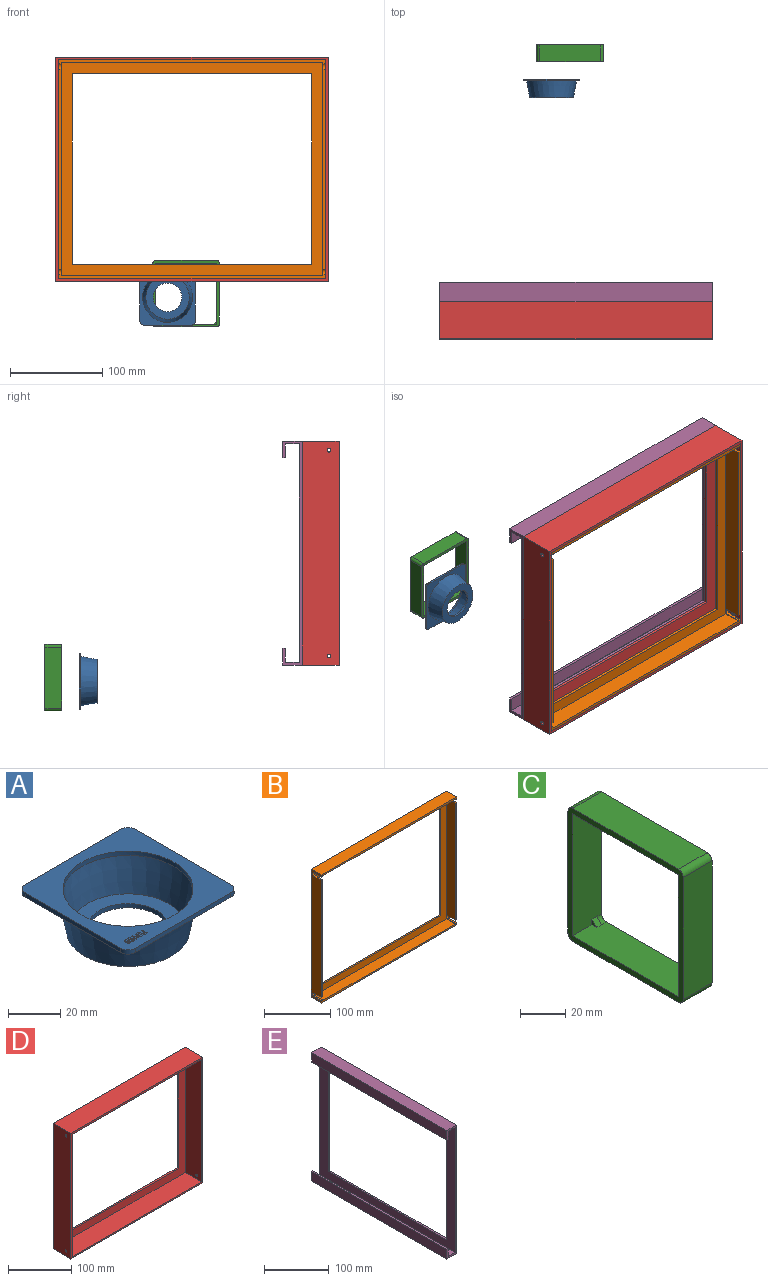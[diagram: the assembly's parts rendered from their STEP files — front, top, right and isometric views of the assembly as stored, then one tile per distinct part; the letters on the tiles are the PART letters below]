
ASSEMBLY  parts=5 mates=4
PART A: 101 faces, bbox 60x60x20 mm
  f0: plane 60x60mm, normal (0,0,1), area 1612.5mm2, adj f1,f2,f3,f4,f5,f7,f8,f9
  f1: plane 52x2mm, normal (1,0,0), area 104mm2, adj f0,f6,f7,f10
  f2: plane 52x2mm, normal (0,1,0), area 104mm2, adj f0,f6,f7,f8
  f3: plane 52x2mm, normal (-1,0,0), area 104mm2, adj f0,f6,f8,f9
  f4: plane 52x2mm, normal (0,-1,0), area 104mm2, adj f0,f6,f9,f10
  f5: cylinder r=25mm len=50mm, axis (0,0,-1), area 314.2mm2, adj f0,f14
  f6: plane 60x60mm, normal (0,0,-1), area 1288.6mm2, adj f1,f2,f3,f4,f7,f8,f9,f10
  f7: cylinder r=4mm len=4mm, axis (0,0,1), area 12.6mm2, adj f0,f1,f2,f6
  f8: cylinder r=4mm len=4mm, axis (0,0,-1), area 12.6mm2, adj f0,f2,f3,f6
  f9: cylinder r=4mm len=4mm, axis (0,0,1), area 12.6mm2, adj f0,f3,f4,f6
  f10: cylinder r=4mm len=4mm, axis (0,0,-1), area 12.6mm2, adj f0,f1,f4,f6
  f11: cylinder r=15.5mm len=31mm, axis (0,0,-1), area 194.8mm2, adj f12,f15
  f12: plane 47.23x47.23mm, normal (0,0,-1), area 996.8mm2, adj f11,f13
  f13: cone r=23.61mm half-angle=10.8deg, axis (0,0,1), area 2908.4mm2, adj f6,f12
  f14: cone r=21.96mm half-angle=10.8deg, axis (0,0,1), area 2396.1mm2, adj f5,f15
  f15: plane 43.92x43.92mm, normal (0,0,1), area 760mm2, adj f11,f14
  f16: extruded ~0.65x0.21mm, area 0.1mm2, adj f0,f17,f34,f35
  f17: extruded ~0.41x0.1mm, area 0mm2, adj f0,f16,f18,f35
  f18: plane 0.79x0.1mm, normal (-1,0.08,0), area 0.1mm2, adj f0,f17,f19,f35
  f19: plane 1.05x0.1mm, normal (0,1,0), area 0.1mm2, adj f0,f18,f20,f35
  f20: plane 0.27x0.1mm, normal (-1,0,0), area 0mm2, adj f0,f19,f21,f35
  f21: plane 1.3x0.1mm, normal (0,-1,0), area 0.1mm2, adj f0,f20,f22,f35
  f22: plane 1.23x0.1mm, normal (1,-0.08,0), area 0.1mm2, adj f0,f21,f23,f35
  f23: plane 0.15x0.1mm, normal (0.54,0.84,0), area 0mm2, adj f0,f22,f24,f35
  f24: extruded ~0.46x0.1mm, area 0mm2, adj f0,f23,f25,f35
  f25: extruded ~0.67x0.55mm, area 0.1mm2, adj f0,f24,f26,f35
  f26: extruded ~0.43x0.17mm, area 0mm2, adj f0,f25,f27,f35
  f27: extruded ~0.49x0.15mm, area 0.1mm2, adj f0,f26,f28,f35
  f28: extruded ~0.37x0.1mm, area 0mm2, adj f0,f27,f29,f35
  f29: extruded ~0.31x0.13mm, area 0mm2, adj f0,f28,f30,f35
  f30: plane 0.29x0.1mm, normal (1,0,0), area 0mm2, adj f0,f29,f31,f35
  f31: extruded ~0.68x0.14mm, area 0.1mm2, adj f0,f30,f32,f35
  f32: extruded ~0.71x0.23mm, area 0.1mm2, adj f0,f31,f33,f35
  f33: extruded ~0.64x0.26mm, area 0.1mm2, adj f0,f32,f34,f35
  f34: extruded ~0.56x0.24mm, area 0.1mm2, adj f0,f16,f33,f35
  f35: plane 2.65x1.65mm, normal (0,0,1), area 1.6mm2, adj f16,f17,f18,f19,f20,f21,f22,f23
  f36: plane 2.32x0.89mm, normal (0.93,0.36,0), area 0.2mm2, adj f0,f37,f53,f54
  f37: plane 0.25x0.1mm, normal (0,1,0), area 0mm2, adj f0,f36,f38,f54
  f38: plane 2.32x0.9mm, normal (-0.93,0.36,0), area 0.2mm2, adj f0,f37,f39,f54
  f39: plane 0.1x0.01mm, normal (0,1,0), area 0mm2, adj f0,f38,f40,f54
  f40: extruded ~0.63x0.1mm, area 0.1mm2, adj f0,f39,f41,f54
  f41: plane 1.69x0.1mm, normal (1,0,0), area 0.2mm2, adj f0,f40,f42,f54
  f42: plane 0.3x0.1mm, normal (0,1,0), area 0mm2, adj f0,f41,f43,f54
  f43: plane 2.62x0.1mm, normal (-1,0,0), area 0.3mm2, adj f0,f42,f44,f54
  f44: plane 0.46x0.1mm, normal (0,-1,0), area 0mm2, adj f0,f43,f45,f54
  f45: plane 2.16x0.84mm, normal (0.93,-0.36,0), area 0.2mm2, adj f0,f44,f46,f54
  f46: plane 0.1x0.01mm, normal (0,-1,0), area 0mm2, adj f0,f45,f47,f54
  f47: plane 2.16x0.83mm, normal (-0.93,-0.36,0), area 0.2mm2, adj f0,f46,f48,f54
  f48: plane 0.46x0.1mm, normal (0,-1,0), area 0mm2, adj f0,f47,f49,f54
  f49: plane 2.62x0.1mm, normal (1,0,0), area 0.3mm2, adj f0,f48,f50,f54
  f50: plane 0.28x0.1mm, normal (0,1,0), area 0mm2, adj f0,f49,f51,f54
  f51: plane 1.67x0.1mm, normal (-1,0,0), area 0.2mm2, adj f0,f50,f52,f54
  f52: extruded ~0.66x0.1mm, area 0.1mm2, adj f0,f51,f53,f54
  f53: plane 0.1x0.01mm, normal (0,1,0), area 0mm2, adj f0,f36,f52,f54
  f54: plane 2.62x2.59mm, normal (0,0,1), area 2.9mm2, adj f36,f37,f38,f39,f40,f41,f42,f43
  f55: plane 2.32x0.89mm, normal (0.93,0.36,0), area 0.2mm2, adj f0,f56,f72,f73
  f56: plane 0.25x0.1mm, normal (0,1,0), area 0mm2, adj f0,f55,f57,f73
  f57: plane 2.32x0.9mm, normal (-0.93,0.36,0), area 0.2mm2, adj f0,f56,f58,f73
  f58: plane 0.1x0.01mm, normal (0,1,0), area 0mm2, adj f0,f57,f59,f73
  f59: extruded ~0.63x0.1mm, area 0.1mm2, adj f0,f58,f60,f73
  f60: plane 1.69x0.1mm, normal (1,0,0), area 0.2mm2, adj f0,f59,f61,f73
  f61: plane 0.3x0.1mm, normal (0,1,0), area 0mm2, adj f0,f60,f62,f73
  f62: plane 2.62x0.1mm, normal (-1,0,0), area 0.3mm2, adj f0,f61,f63,f73
  f63: plane 0.46x0.1mm, normal (0,-1,0), area 0mm2, adj f0,f62,f64,f73
  f64: plane 2.16x0.84mm, normal (0.93,-0.36,0), area 0.2mm2, adj f0,f63,f65,f73
  f65: plane 0.1x0.01mm, normal (0,-1,0), area 0mm2, adj f0,f64,f66,f73
  f66: plane 2.16x0.83mm, normal (-0.93,-0.36,0), area 0.2mm2, adj f0,f65,f67,f73
  f67: plane 0.46x0.1mm, normal (0,-1,0), area 0mm2, adj f0,f66,f68,f73
  f68: plane 2.62x0.1mm, normal (1,0,0), area 0.3mm2, adj f0,f67,f69,f73
  f69: plane 0.28x0.1mm, normal (0,1,0), area 0mm2, adj f0,f68,f70,f73
  f70: plane 1.67x0.1mm, normal (-1,0,0), area 0.2mm2, adj f0,f69,f71,f73
  f71: extruded ~0.66x0.1mm, area 0.1mm2, adj f0,f70,f72,f73
  f72: plane 0.1x0.01mm, normal (0,1,0), area 0mm2, adj f0,f55,f71,f73
  f73: plane 2.62x2.59mm, normal (0,0,1), area 2.9mm2, adj f55,f56,f57,f58,f59,f60,f61,f62
  f74: extruded ~0.39x0.16mm, area 0mm2, adj f75,f98,f99,f100
  f75: extruded ~0.3x0.1mm, area 0mm2, adj f74,f76,f99,f100
  f76: extruded ~0.25x0.2mm, area 0mm2, adj f75,f77,f99,f100
  f77: extruded ~0.34x0.1mm, area 0mm2, adj f76,f78,f99,f100
  f78: extruded ~0.24x0.1mm, area 0mm2, adj f77,f79,f99,f100
  f79: extruded ~0.21x0.18mm, area 0mm2, adj f78,f80,f99,f100
  f80: extruded ~0.3x0.1mm, area 0mm2, adj f79,f81,f99,f100
  f81: extruded ~0.39x0.15mm, area 0mm2, adj f80,f82,f99,f100
  f82: extruded ~0.41x0.13mm, area 0mm2, adj f81,f98,f99,f100
  f83: extruded ~1.15x0.3mm, area 0.1mm2, adj f0,f84,f97,f99
  f84: extruded ~0.85x0.24mm, area 0.1mm2, adj f0,f83,f85,f99
  f85: extruded ~0.64x0.31mm, area 0.1mm2, adj f0,f84,f86,f99
  f86: extruded ~0.6x0.23mm, area 0.1mm2, adj f0,f85,f87,f99
  f87: extruded ~0.64x0.22mm, area 0.1mm2, adj f0,f86,f88,f99
  f88: extruded ~0.58x0.2mm, area 0.1mm2, adj f0,f87,f89,f99
  f89: extruded ~0.56x0.21mm, area 0.1mm2, adj f0,f88,f90,f99
  f90: extruded ~0.62x0.31mm, area 0.1mm2, adj f0,f89,f91,f99
  f91: plane 0.1x0.02mm, normal (0,-1,0), area 0mm2, adj f0,f90,f92,f99
  f92: extruded ~0.83x0.24mm, area 0.1mm2, adj f0,f91,f93,f99
  f93: extruded ~0.64x0.26mm, area 0.1mm2, adj f0,f92,f94,f99
  f94: extruded ~0.32x0.1mm, area 0mm2, adj f0,f93,f95,f99
  f95: plane 0.26x0.1mm, normal (-1,0,0), area 0mm2, adj f0,f94,f96,f99
  f96: extruded ~0.32x0.1mm, area 0mm2, adj f0,f95,f97,f99
  f97: extruded ~0.89x0.38mm, area 0.1mm2, adj f0,f83,f96,f99
  f98: extruded ~0.46x0.14mm, area 0mm2, adj f74,f82,f99,f100
  f99: plane 2.69x1.71mm, normal (0,0,1), area 1.8mm2, adj f74,f75,f76,f77,f78,f79,f80,f81
  f100: plane 1.18x1.11mm, normal (0,0,1), area 1.1mm2, adj f74,f75,f76,f77,f78,f79,f80,f81
PART B: 126 faces, bbox 289.3x22x236.8 mm
  f0: plane 289.28x4mm, normal (0,-1,0), area 873.8mm2, adj f3,f4,f13,f30,f41,f44,f69,f109
  f1: plane 216.71x3mm, normal (0,-1,0), area 650.1mm2, adj f3,f5,f90,f107
  f2: plane 216.71x3mm, normal (0,-1,0), area 650.1mm2, adj f4,f22,f50,f87
  f3: plane 236.78x22mm, normal (1,0,0), area 4975mm2, adj f0,f1,f39,f40,f41,f42,f88,f89
  f4: plane 236.78x22mm, normal (-1,0,0), area 4975mm2, adj f0,f2,f39,f40,f41,f42,f50,f51
  f5: plane 230.78x19mm, normal (-1,0,0), area 4134.3mm2, adj f1,f43,f44,f45,f88,f89,f90,f107
  f6: plane 2x1mm, normal (-1,0,0), area 1mm2, adj f44,f111,f112
  f7: plane 2x1mm, normal (-1,0,0), area 1mm2, adj f44,f113,f114
  f8: plane 2x1mm, normal (-1,0,0), area 1mm2, adj f44,f115,f116
  f9: plane 2x1mm, normal (-1,0,0), area 1mm2, adj f44,f117,f118
  f10: plane 2x1mm, normal (-1,0,0), area 1mm2, adj f44,f119,f120
  f11: plane 2x1mm, normal (-1,0,0), area 1mm2, adj f44,f121,f122
  f12: plane 2x1mm, normal (-1,0,0), area 1mm2, adj f44,f123,f124
  f13: plane 1.65x1mm, normal (-1,0,0), area 1.2mm2, adj f0,f44,f109,f125
  f14: plane 1.65x1mm, normal (-1,0,0), area 1.2mm2, adj f39,f43,f91,f92
  f15: plane 2x1mm, normal (-1,0,0), area 1mm2, adj f43,f93,f94
  f16: plane 2x1mm, normal (-1,0,0), area 1mm2, adj f43,f95,f96
  f17: plane 2x1mm, normal (-1,0,0), area 1mm2, adj f43,f97,f98
  f18: plane 2x1mm, normal (-1,0,0), area 1mm2, adj f43,f99,f100
  f19: plane 2x1mm, normal (-1,0,0), area 1mm2, adj f43,f101,f102
  f20: plane 2x1mm, normal (-1,0,0), area 1mm2, adj f43,f103,f104
  f21: plane 2x1mm, normal (-1,0,0), area 1mm2, adj f43,f105,f106
  f22: plane 230.78x19mm, normal (1,0,0), area 4134.3mm2, adj f2,f43,f44,f45,f50,f51,f68,f85
  f23: plane 2x1mm, normal (1,0,0), area 1mm2, adj f44,f83,f84
  f24: plane 2x1mm, normal (1,0,0), area 1mm2, adj f44,f81,f82
  f25: plane 2x1mm, normal (1,0,0), area 1mm2, adj f44,f79,f80
  f26: plane 2x1mm, normal (1,0,0), area 1mm2, adj f44,f77,f78
  f27: plane 2x1mm, normal (1,0,0), area 1mm2, adj f44,f75,f76
  f28: plane 2x1mm, normal (1,0,0), area 1mm2, adj f44,f73,f74
  f29: plane 2x1mm, normal (1,0,0), area 1mm2, adj f44,f71,f72
  f30: plane 1.65x1mm, normal (1,0,0), area 1.2mm2, adj f0,f44,f69,f70
  f31: plane 1.65x1mm, normal (1,0,0), area 1.2mm2, adj f39,f43,f66,f67
  f32: plane 2x1mm, normal (1,0,0), area 1mm2, adj f43,f64,f65
  f33: plane 2x1mm, normal (1,0,0), area 1mm2, adj f43,f62,f63
  f34: plane 2x1mm, normal (1,0,0), area 1mm2, adj f43,f60,f61
  f35: plane 2x1mm, normal (1,0,0), area 1mm2, adj f43,f58,f59
  f36: plane 2x1mm, normal (1,0,0), area 1mm2, adj f43,f56,f57
  f37: plane 2x1mm, normal (1,0,0), area 1mm2, adj f43,f54,f55
  f38: plane 2x1mm, normal (1,0,0), area 1mm2, adj f43,f52,f53
  f39: plane 289.28x4mm, normal (0,-1,0), area 873.8mm2, adj f3,f4,f14,f31,f40,f43,f67,f91
  f40: plane 289.28x22mm, normal (0,0,1), area 6364.1mm2, adj f3,f4,f39,f42
  f41: plane 289.28x22mm, normal (0,0,-1), area 6364.1mm2, adj f0,f3,f4,f42
  f42: plane 289.28x236.78mm, normal (0,1,0), area 14881.6mm2, adj f3,f4,f40,f41,f46,f47,f48,f49
  f43: plane 283.28x19mm, normal (0,0,-1), area 5382.2mm2, adj f5,f14,f15,f16,f17,f18,f19,f20
  f44: plane 283.28x19mm, normal (0,0,1), area 5382.2mm2, adj f0,f5,f6,f7,f8,f9,f10,f11
  f45: plane 283.28x230.78mm, normal (0,-1,0), area 11761.3mm2, adj f5,f22,f43,f44,f46,f47,f48,f49
  f46: plane 206.78x3mm, normal (-1,0,0), area 620.3mm2, adj f42,f45,f47,f49
  f47: plane 259.28x3mm, normal (0,0,-1), area 777.8mm2, adj f42,f45,f46,f48
  f48: plane 206.78x3mm, normal (1,0,0), area 620.3mm2, adj f42,f45,f47,f49
  f49: plane 259.28x3mm, normal (0,0,1), area 777.8mm2, adj f42,f45,f46,f48
  f50: plane 16.65x3mm, normal (0,0,1), area 50mm2, adj f2,f4,f22,f51
  f51: cylinder r=3.3mm len=6.04mm, axis (-1,0,0), area 22.9mm2, adj f4,f22,f50,f68
  f52: plane 3x1mm, normal (0,0.71,-0.71), area 4.2mm2, adj f4,f38,f53,f68
  f53: plane 3x1mm, normal (0,-0.71,-0.71), area 4.2mm2, adj f4,f38,f52,f54
  f54: plane 3x1mm, normal (0,0.71,-0.71), area 4.2mm2, adj f4,f37,f53,f55
  f55: plane 3x1mm, normal (0,-0.71,-0.71), area 4.2mm2, adj f4,f37,f54,f56
  f56: plane 3x1mm, normal (0,0.71,-0.71), area 4.2mm2, adj f4,f36,f55,f57
  f57: plane 3x1mm, normal (0,-0.71,-0.71), area 4.2mm2, adj f4,f36,f56,f58
  f58: plane 3x1mm, normal (0,0.71,-0.71), area 4.2mm2, adj f4,f35,f57,f59
  f59: plane 3x1mm, normal (0,-0.71,-0.71), area 4.2mm2, adj f4,f35,f58,f60
  f60: plane 3x1mm, normal (0,0.71,-0.71), area 4.2mm2, adj f4,f34,f59,f61
  f61: plane 3x1mm, normal (0,-0.71,-0.71), area 4.2mm2, adj f4,f34,f60,f62
  f62: plane 3x1mm, normal (0,0.71,-0.71), area 4.2mm2, adj f4,f33,f61,f63
  f63: plane 3x1mm, normal (0,-0.71,-0.71), area 4.2mm2, adj f4,f33,f62,f64
  f64: plane 3x1mm, normal (0,0.71,-0.71), area 4.2mm2, adj f4,f32,f63,f65
  f65: plane 3x1mm, normal (0,-0.71,-0.71), area 4.2mm2, adj f4,f32,f64,f66
  f66: plane 3x1mm, normal (0,0.71,-0.71), area 4.2mm2, adj f4,f31,f65,f67
  f67: plane 3x0.65mm, normal (0,0,-1), area 2mm2, adj f4,f31,f39,f66
  f68: plane 3x1mm, normal (0,-0.71,-0.71), area 4.2mm2, adj f4,f22,f51,f52
  f69: plane 3x0.65mm, normal (0,0,1), area 2mm2, adj f0,f4,f30,f70
  f70: plane 3x1mm, normal (0,0.71,0.71), area 4.2mm2, adj f4,f30,f69,f71
  f71: plane 3x1mm, normal (0,-0.71,0.71), area 4.2mm2, adj f4,f29,f70,f72
  f72: plane 3x1mm, normal (0,0.71,0.71), area 4.2mm2, adj f4,f29,f71,f73
  f73: plane 3x1mm, normal (0,-0.71,0.71), area 4.2mm2, adj f4,f28,f72,f74
  f74: plane 3x1mm, normal (0,0.71,0.71), area 4.2mm2, adj f4,f28,f73,f75
  f75: plane 3x1mm, normal (0,-0.71,0.71), area 4.2mm2, adj f4,f27,f74,f76
  f76: plane 3x1mm, normal (0,0.71,0.71), area 4.2mm2, adj f4,f27,f75,f77
  f77: plane 3x1mm, normal (0,-0.71,0.71), area 4.2mm2, adj f4,f26,f76,f78
  f78: plane 3x1mm, normal (0,0.71,0.71), area 4.2mm2, adj f4,f26,f77,f79
  f79: plane 3x1mm, normal (0,-0.71,0.71), area 4.2mm2, adj f4,f25,f78,f80
  f80: plane 3x1mm, normal (0,0.71,0.71), area 4.2mm2, adj f4,f25,f79,f81
  f81: plane 3x1mm, normal (0,-0.71,0.71), area 4.2mm2, adj f4,f24,f80,f82
  f82: plane 3x1mm, normal (0,0.71,0.71), area 4.2mm2, adj f4,f24,f81,f83
  f83: plane 3x1mm, normal (0,-0.71,0.71), area 4.2mm2, adj f4,f23,f82,f84
  f84: plane 3x1mm, normal (0,0.71,0.71), area 4.2mm2, adj f4,f23,f83,f85
  f85: plane 3x1mm, normal (0,-0.71,0.71), area 4.2mm2, adj f4,f22,f84,f86
  f86: cylinder r=3.3mm len=6.04mm, axis (-1,0,0), area 22.9mm2, adj f4,f22,f85,f87
  f87: plane 16.65x3mm, normal (0,0,-1), area 50mm2, adj f2,f4,f22,f86
  f88: plane 3x1mm, normal (0,-0.71,-0.71), area 4.2mm2, adj f3,f5,f89,f106
  f89: cylinder r=3.3mm len=6.04mm, axis (-1,0,0), area 22.9mm2, adj f3,f5,f88,f90
  f90: plane 16.65x3mm, normal (0,0,1), area 50mm2, adj f1,f3,f5,f89
  f91: plane 3x0.65mm, normal (0,0,-1), area 2mm2, adj f3,f14,f39,f92
  f92: plane 3x1mm, normal (0,0.71,-0.71), area 4.2mm2, adj f3,f14,f91,f93
  f93: plane 3x1mm, normal (0,-0.71,-0.71), area 4.2mm2, adj f3,f15,f92,f94
  f94: plane 3x1mm, normal (0,0.71,-0.71), area 4.2mm2, adj f3,f15,f93,f95
  f95: plane 3x1mm, normal (0,-0.71,-0.71), area 4.2mm2, adj f3,f16,f94,f96
  f96: plane 3x1mm, normal (0,0.71,-0.71), area 4.2mm2, adj f3,f16,f95,f97
  f97: plane 3x1mm, normal (0,-0.71,-0.71), area 4.2mm2, adj f3,f17,f96,f98
  f98: plane 3x1mm, normal (0,0.71,-0.71), area 4.2mm2, adj f3,f17,f97,f99
  f99: plane 3x1mm, normal (0,-0.71,-0.71), area 4.2mm2, adj f3,f18,f98,f100
  f100: plane 3x1mm, normal (0,0.71,-0.71), area 4.2mm2, adj f3,f18,f99,f101
  f101: plane 3x1mm, normal (0,-0.71,-0.71), area 4.2mm2, adj f3,f19,f100,f102
  f102: plane 3x1mm, normal (0,0.71,-0.71), area 4.2mm2, adj f3,f19,f101,f103
  f103: plane 3x1mm, normal (0,-0.71,-0.71), area 4.2mm2, adj f3,f20,f102,f104
  f104: plane 3x1mm, normal (0,0.71,-0.71), area 4.2mm2, adj f3,f20,f103,f105
  f105: plane 3x1mm, normal (0,-0.71,-0.71), area 4.2mm2, adj f3,f21,f104,f106
  f106: plane 3x1mm, normal (0,0.71,-0.71), area 4.2mm2, adj f3,f21,f88,f105
  f107: plane 16.65x3mm, normal (0,0,-1), area 50mm2, adj f1,f3,f5,f108
  f108: cylinder r=3.3mm len=6.04mm, axis (-1,0,0), area 22.9mm2, adj f3,f5,f107,f110
  f109: plane 3x0.65mm, normal (0,0,1), area 2mm2, adj f0,f3,f13,f125
  f110: plane 3x1mm, normal (0,-0.71,0.71), area 4.2mm2, adj f3,f5,f108,f111
  f111: plane 3x1mm, normal (0,0.71,0.71), area 4.2mm2, adj f3,f6,f110,f112
  f112: plane 3x1mm, normal (0,-0.71,0.71), area 4.2mm2, adj f3,f6,f111,f113
  f113: plane 3x1mm, normal (0,0.71,0.71), area 4.2mm2, adj f3,f7,f112,f114
  f114: plane 3x1mm, normal (0,-0.71,0.71), area 4.2mm2, adj f3,f7,f113,f115
  f115: plane 3x1mm, normal (0,0.71,0.71), area 4.2mm2, adj f3,f8,f114,f116
  f116: plane 3x1mm, normal (0,-0.71,0.71), area 4.2mm2, adj f3,f8,f115,f117
  f117: plane 3x1mm, normal (0,0.71,0.71), area 4.2mm2, adj f3,f9,f116,f118
  f118: plane 3x1mm, normal (0,-0.71,0.71), area 4.2mm2, adj f3,f9,f117,f119
  f119: plane 3x1mm, normal (0,0.71,0.71), area 4.2mm2, adj f3,f10,f118,f120
  f120: plane 3x1mm, normal (0,-0.71,0.71), area 4.2mm2, adj f3,f10,f119,f121
  f121: plane 3x1mm, normal (0,0.71,0.71), area 4.2mm2, adj f3,f11,f120,f122
  f122: plane 3x1mm, normal (0,-0.71,0.71), area 4.2mm2, adj f3,f11,f121,f123
  f123: plane 3x1mm, normal (0,0.71,0.71), area 4.2mm2, adj f3,f12,f122,f124
  f124: plane 3x1mm, normal (0,-0.71,0.71), area 4.2mm2, adj f3,f12,f123,f125
  f125: plane 3x1mm, normal (0,0.71,0.71), area 4.2mm2, adj f3,f13,f109,f124
PART C: 30 faces, bbox 18x72x72 mm
  f0: plane 3x3mm, normal (-1,0,0), area 4.5mm2, adj f12,f15,f29
  f1: plane 3x3mm, normal (-1,0,0), area 4.5mm2, adj f12,f13,f28
  f2: plane 3x3mm, normal (-1,0,0), area 4.5mm2, adj f13,f14,f27
  f3: plane 3x3mm, normal (1,0,0), area 2.6mm2, adj f19,f26
  f4: plane 3x3mm, normal (1,0,0), area 2.6mm2, adj f20,f27
  f5: plane 3x3mm, normal (1,0,0), area 2.6mm2, adj f21,f28
  f6: plane 66x18mm, normal (0,1,0), area 1188mm2, adj f10,f11,f22,f25
  f7: plane 66x18mm, normal (0,0,1), area 1188mm2, adj f10,f11,f22,f23
  f8: plane 66x18mm, normal (0,-1,0), area 1188mm2, adj f10,f11,f23,f24
  f9: plane 66x18mm, normal (0,0,-1), area 1188mm2, adj f10,f11,f24,f25
  f10: plane 72x72mm, normal (1,0,0), area 828mm2, adj f6,f7,f8,f9,f12,f13,f14,f15
  f11: plane 72x72mm, normal (-1,0,0), area 820.3mm2, adj f6,f7,f8,f9,f12,f13,f14,f15
  f12: plane 66x18mm, normal (0,-1,0), area 1152mm2, adj f0,f1,f10,f11,f13,f15,f18,f21
  f13: plane 66x18mm, normal (0,0,1), area 1152mm2, adj f1,f2,f10,f11,f12,f14,f20,f21
  f14: plane 66x18mm, normal (0,1,0), area 1152mm2, adj f2,f10,f11,f13,f15,f16,f19,f20
  f15: plane 66x18mm, normal (0,0,-1), area 1152mm2, adj f0,f10,f11,f12,f14,f16,f18,f19
  f16: plane 3x3mm, normal (-1,0,0), area 4.5mm2, adj f14,f15,f26
  f17: plane 3x3mm, normal (1,0,0), area 2.6mm2, adj f18,f29
  f18: cylinder r=3mm len=3mm, axis (-1,0,0), area 14.1mm2, adj f10,f12,f15,f17
  f19: cylinder r=3mm len=3mm, axis (-1,0,0), area 14.1mm2, adj f3,f10,f14,f15
  f20: cylinder r=3mm len=3mm, axis (-1,0,0), area 14.1mm2, adj f4,f10,f13,f14
  f21: cylinder r=3mm len=3mm, axis (-1,0,0), area 14.1mm2, adj f5,f10,f12,f13
  f22: cylinder r=3mm len=18mm, axis (1,0,0), area 84.8mm2, adj f6,f7,f10,f11
  f23: cylinder r=3mm len=18mm, axis (-1,0,0), area 84.8mm2, adj f7,f8,f10,f11
  f24: cylinder r=3mm len=18mm, axis (1,0,0), area 84.8mm2, adj f8,f9,f10,f11
  f25: cylinder r=3mm len=18mm, axis (-1,0,0), area 84.8mm2, adj f6,f9,f10,f11
  f26: plane 3x3mm, normal (0,0.71,-0.71), area 12.7mm2, adj f3,f14,f15,f16
  f27: plane 3x3mm, normal (0,0.71,0.71), area 12.7mm2, adj f2,f4,f13,f14
  f28: plane 3x3mm, normal (0,-0.71,0.71), area 12.7mm2, adj f1,f5,f12,f13
  f29: plane 3x3mm, normal (0,-0.71,-0.71), area 12.7mm2, adj f0,f12,f15,f17
PART D: 19 faces, bbox 295.3x40x242.8 mm
  f0: plane 295.28x242.78mm, normal (0,-1,0), area 3192.3mm2, adj f1,f2,f3,f4,f6,f7,f8,f9
  f1: plane 242.78x40mm, normal (1,0,0), area 9686mm2, adj f0,f2,f4,f5,f17,f18
  f2: plane 295.28x40mm, normal (0,0,1), area 11811mm2, adj f0,f1,f3,f5
  f3: plane 242.78x40mm, normal (-1,0,0), area 9686mm2, adj f0,f2,f4,f5,f15,f16
  f4: plane 295.28x40mm, normal (0,0,-1), area 11811mm2, adj f0,f1,f3,f5
  f5: plane 295.28x242.78mm, normal (0,1,0), area 18073.9mm2, adj f1,f2,f3,f4,f11,f12,f13,f14
  f6: plane 236.78x37mm, normal (-1,0,0), area 8735.7mm2, adj f0,f7,f9,f10,f17,f18
  f7: plane 289.28x37mm, normal (0,0,-1), area 10703.2mm2, adj f0,f6,f8,f10
  f8: plane 236.78x37mm, normal (1,0,0), area 8735.7mm2, adj f0,f7,f9,f10,f15,f16
  f9: plane 289.28x37mm, normal (0,0,1), area 10703.2mm2, adj f0,f6,f8,f10
  f10: plane 289.28x236.78mm, normal (0,-1,0), area 14881.6mm2, adj f6,f7,f8,f9,f11,f12,f13,f14
  f11: plane 206.78x3mm, normal (-1,0,0), area 620.3mm2, adj f5,f10,f12,f14
  f12: plane 259.28x3mm, normal (0,0,-1), area 777.8mm2, adj f5,f10,f11,f13
  f13: plane 206.78x3mm, normal (1,0,0), area 620.3mm2, adj f5,f10,f12,f14
  f14: plane 259.28x3mm, normal (0,0,1), area 777.8mm2, adj f5,f10,f11,f13
  f15: cylinder r=2mm len=4mm, axis (-1,0,0), area 37.7mm2, adj f3,f8
  f16: cylinder r=2mm len=4mm, axis (-1,0,0), area 37.7mm2, adj f3,f8
  f17: cylinder r=2mm len=4mm, axis (-1,0,0), area 37.7mm2, adj f1,f6
  f18: cylinder r=2mm len=4mm, axis (-1,0,0), area 37.7mm2, adj f1,f6
PART E: 18 faces, bbox 21.1x295.3x242.8 mm
  f0: plane 295.28x242.78mm, normal (1,0,0), area 18073.9mm2, adj f1,f11,f12,f13,f14,f15,f16,f17
  f1: plane 295.28x21.1mm, normal (0,0,1), area 6230.3mm2, adj f0,f2,f12,f13
  f2: plane 295.28x18mm, normal (-1,0,0), area 5314.9mm2, adj f1,f3,f12,f13
  f3: plane 295.28x3mm, normal (0,0,-1), area 885.8mm2, adj f2,f4,f12,f13
  f4: plane 295.28x15mm, normal (1,0,0), area 4429.1mm2, adj f3,f5,f12,f13
  f5: plane 295.28x15.1mm, normal (0,0,-1), area 4458.7mm2, adj f4,f6,f12,f13
  f6: plane 295.28x236.78mm, normal (-1,0,0), area 16302.3mm2, adj f5,f7,f12,f13,f14,f15,f16,f17
  f7: plane 295.28x15.1mm, normal (0,0,1), area 4458.7mm2, adj f6,f8,f12,f13
  f8: plane 295.28x15mm, normal (1,0,0), area 4429.1mm2, adj f7,f9,f12,f13
  f9: plane 295.28x3mm, normal (0,0,1), area 885.8mm2, adj f8,f10,f12,f13
  f10: plane 295.28x18mm, normal (-1,0,0), area 5314.9mm2, adj f9,f11,f12,f13
  f11: plane 295.28x21.1mm, normal (0,0,-1), area 6230.3mm2, adj f0,f10,f12,f13
  f12: plane 242.78x21.1mm, normal (0,-1,0), area 926.9mm2, adj f0,f1,f2,f3,f4,f5,f6,f7
  f13: plane 242.78x21.1mm, normal (0,1,0), area 926.9mm2, adj f0,f1,f2,f3,f4,f5,f6,f7
  f14: plane 259.28x3mm, normal (0,0,-1), area 777.8mm2, adj f0,f6,f15,f17
  f15: plane 206.78x3mm, normal (0,-1,0), area 620.3mm2, adj f0,f6,f14,f16
  f16: plane 259.28x3mm, normal (0,0,1), area 777.8mm2, adj f0,f6,f15,f17
  f17: plane 206.78x3mm, normal (0,1,0), area 620.3mm2, adj f0,f6,f14,f16
PLACE A rot(axis=(0,-0.71,-0.71),180deg) t=(-14.44,184.9,-136.02)mm
PLACE B t=(12,-73,3)mm
PLACE C rot(axis=(0,0,1),90deg) t=(5.56,205.9,-132.02)mm
PLACE D t=(12,-55,3)mm
PLACE E rot(axis=(0,0,-1),90deg) t=(12,-52,3)mm
MATE parallel A.f9 <-> C.f20  axis (0,-1,0) through (11.56,184.9,-162.02)mm
MATE parallel E.f12 <-> D.f3  axis (-1,0,0) through (-135.64,-55,-118.39)mm
MATE parallel B.f3 <-> D.f6  axis (-1,0,0) through (156.64,-95,-115.39)mm
MATE parallel D.f3 <-> E.f12  axis (-1,0,0) through (-135.64,-55,-118.39)mm
